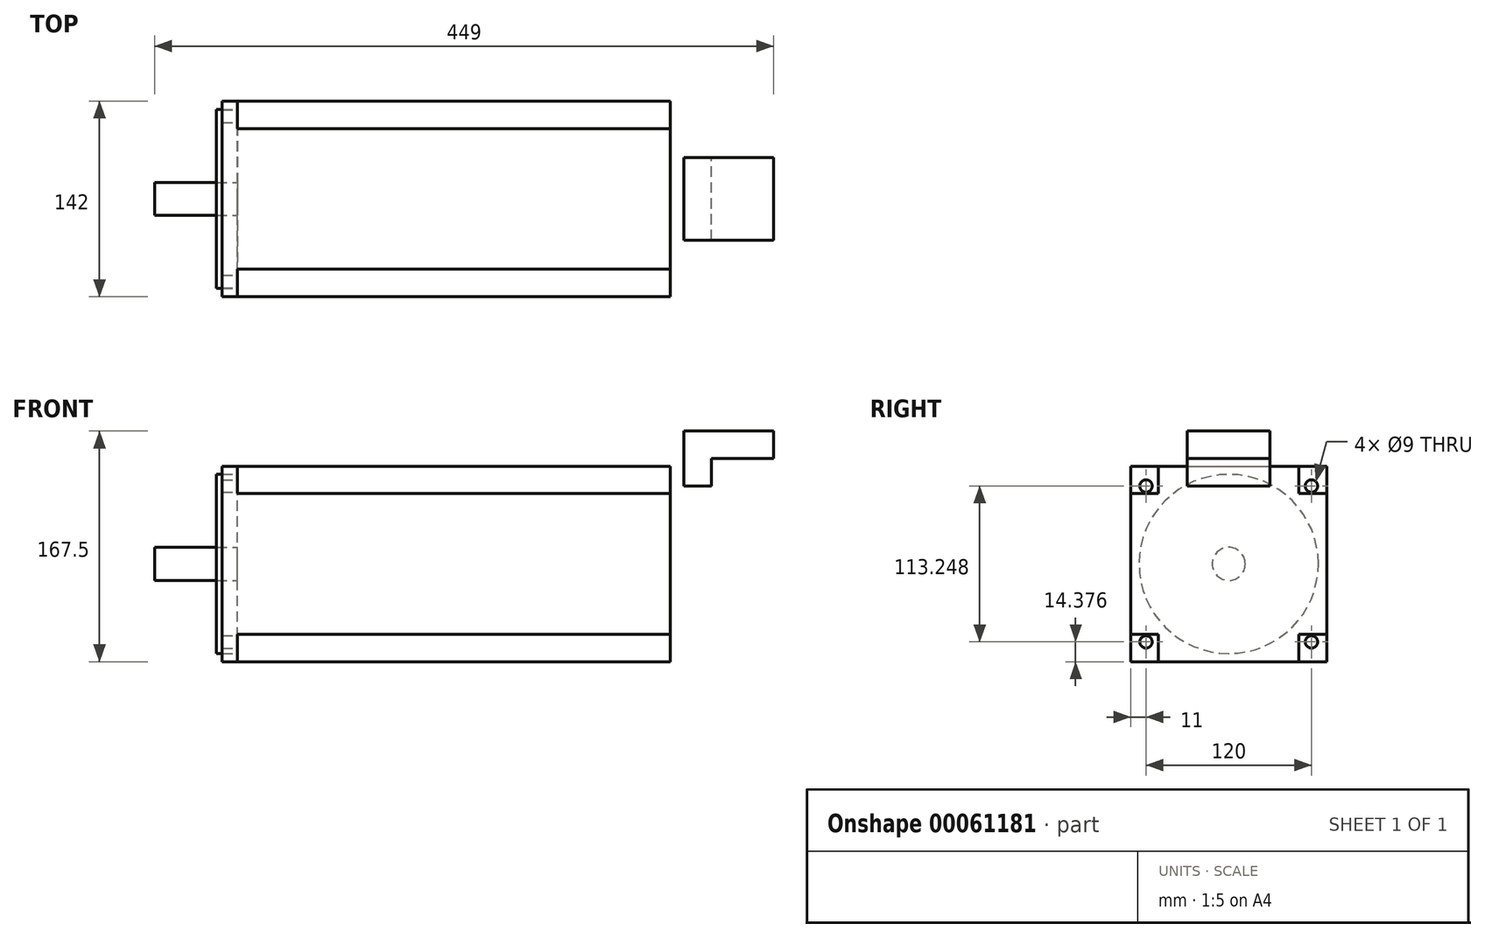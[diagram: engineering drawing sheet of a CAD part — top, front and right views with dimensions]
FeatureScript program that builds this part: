
annotation { "Feature Type Name" : "Feature", "Feature Type Description" : "" }
export const myFeature = defineFeature(function(context is Context, id is Id, definition is map)
    precondition{}
    {
        {
            var Q0;
            Q0=qCreatedBy(makeId("Right.planeOp"),FACE);
            var sketch = newSketch(context, id + "F6", { "sketchPlane" : qUnion([Q0])});
            skLineSegment(sketch, "E0.bottom", {"start": v(-71, -71) * mm, "end": v(71, -71) * mm});
            skLineSegment(sketch, "E0.top", {"start": v(-71, 71) * mm, "end": v(71, 71) * mm});
            skLineSegment(sketch, "E0.left", {"start": v(-71, -71) * mm, "end": v(-71, 71) * mm});
            skLineSegment(sketch, "E0.right", {"start": v(71, -71) * mm, "end": v(71, 71) * mm});
            skLineSegment(sketch, "E1.bottom", {"start": v(-60, -56.62) * mm, "end": v(60, -56.62) * mm, "construction": true});
            skLineSegment(sketch, "E1.top", {"start": v(-60, 56.62) * mm, "end": v(60, 56.62) * mm, "construction": true});
            skLineSegment(sketch, "E1.left", {"start": v(-60, -56.62) * mm, "end": v(-60, 56.62) * mm, "construction": true});
            skLineSegment(sketch, "E1.right", {"start": v(60, -56.62) * mm, "end": v(60, 56.62) * mm, "construction": true});
            skCircle(sketch, "E2", {"center": v(-60, 56.62) * mm, "radius": 4.5 * mm});
            skCircle(sketch, "E3", {"center": v(60, 56.62) * mm, "radius": 4.5 * mm});
            skCircle(sketch, "E4", {"center": v(-60, -56.62) * mm, "radius": 4.5 * mm});
            skCircle(sketch, "E5", {"center": v(60, -56.62) * mm, "radius": 4.5 * mm});
            skCircle(sketch, "E6", {"center": v(0, 0) * mm, "radius": 82.5 * mm, "construction": true});
            skSolve(sketch);
        }
        {
            var Q0;
            Q0=qCreatedBy(makeId("Right.planeOp"),FACE);
            var sketch = newSketch(context, id + "F0", { "sketchPlane" : qUnion([Q0])});
            skLineSegment(sketch, "E7.bottom", {"start": v(-51, -71) * mm, "end": v(51, -71) * mm});
            skLineSegment(sketch, "E7.top", {"start": v(-51, 71) * mm, "end": v(51, 71) * mm});
            skLineSegment(sketch, "E7.left", {"start": v(-51, -71) * mm, "end": v(-51, -51) * mm});
            skLineSegment(sketch, "E7.right", {"start": v(51, -71) * mm, "end": v(51, -51) * mm});
            skLineSegment(sketch, "E8.bottom", {"start": v(71, 51) * mm, "end": v(51, 51) * mm});
            skLineSegment(sketch, "E8.top", {"start": v(71, -51) * mm, "end": v(51, -51) * mm});
            skLineSegment(sketch, "E8.left", {"start": v(71, 51) * mm, "end": v(71, -51) * mm});
            skLineSegment(sketch, "E8.right", {"start": v(-71, 51) * mm, "end": v(-71, -51) * mm});
            skLineSegment(sketch, "E9.trimOffspring", {"start": v(51, 51) * mm, "end": v(51, 71) * mm});
            skLineSegment(sketch, "E10.trimOffspring", {"start": v(-51, -51) * mm, "end": v(-71, -51) * mm});
            skLineSegment(sketch, "E11.trimOffspring", {"start": v(-51, 51) * mm, "end": v(-51, 71) * mm});
            skLineSegment(sketch, "E12.trimOffspring", {"start": v(-51, 51) * mm, "end": v(-71, 51) * mm});
            skSolve(sketch);
        }
        {
            var Q0;
            Q0=qSketchRegion(id+"F0",true);
            extrude(context, id + "F1", {"entities" : qUnion([Q0]), "depth" : 314 * mm});
        }
        {
            var Q0;
            Q0=qSketchRegion(id+"F6",true);
            extrude(context, id + "F2", {"entities" : qUnion([Q0]), "operationType" : NewBodyOperationType.ADD, "oppositeDirection" : true, "depth" : 11 * mm});
        }
        {
            var Q0;
            Q0=qCreatedBy(makeId("Right.planeOp"),FACE);
            var sketch = newSketch(context, id + "F3", { "sketchPlane" : qUnion([Q0])});
            skCircle(sketch, "E13", {"center": v(0, 0) * mm, "radius": 12 * mm});
            skSolve(sketch);
        }
        {
            var Q0;
            Q0=qSketchRegion(id+"F3",true);
            extrude(context, id + "F7", {"entities" : qUnion([Q0]), "oppositeDirection" : true, "depth" : 60 * mm});
        }
        {
            var Q0;
            Q0=qCreatedBy(makeId("Right.planeOp"),FACE);
            var sketch = newSketch(context, id + "F8", { "sketchPlane" : qUnion([Q0])});
            skCircle(sketch, "E14", {"center": v(0, 0) * mm, "radius": 65 * mm});
            skSolve(sketch);
        }
        {
            var Q0;
            Q0=qSketchRegion(id+"F8",true);
            extrude(context, id + "F4", {"entities" : qUnion([Q0]), "oppositeDirection" : true, "depth" : 15 * mm});
        }
        {
            var Q0;
            Q0=qCreatedBy(makeId("Front.planeOp"),FACE);
            var sketch = newSketch(context, id + "F9", { "sketchPlane" : qUnion([Q0])});
            skLineSegment(sketch, "E15.bottom", {"start": v(324, 56.5) * mm, "end": v(344, 56.5) * mm});
            skLineSegment(sketch, "E15.left", {"start": v(324, 56.5) * mm, "end": v(324, 76.5) * mm});
            skLineSegment(sketch, "E15.right", {"start": v(344, 56.5) * mm, "end": v(344, 76.5) * mm});
            skLineSegment(sketch, "E16.bottom", {"start": v(344, 76.5) * mm, "end": v(389, 76.5) * mm});
            skLineSegment(sketch, "E16.top", {"start": v(324, 96.5) * mm, "end": v(389, 96.5) * mm});
            skLineSegment(sketch, "E16.left", {"start": v(324, 76.5) * mm, "end": v(324, 96.5) * mm});
            skLineSegment(sketch, "E16.right", {"start": v(389, 76.5) * mm, "end": v(389, 96.5) * mm});
            skSolve(sketch);
        }
        {
            var Q0;
            Q0=qSketchRegion(id+"F9",true);
            extrude(context, id + "F5", {"entities" : qUnion([Q0]), "endBound" : BoundingType.SYMMETRIC, "depth" : 60 * mm});
        }
    });
